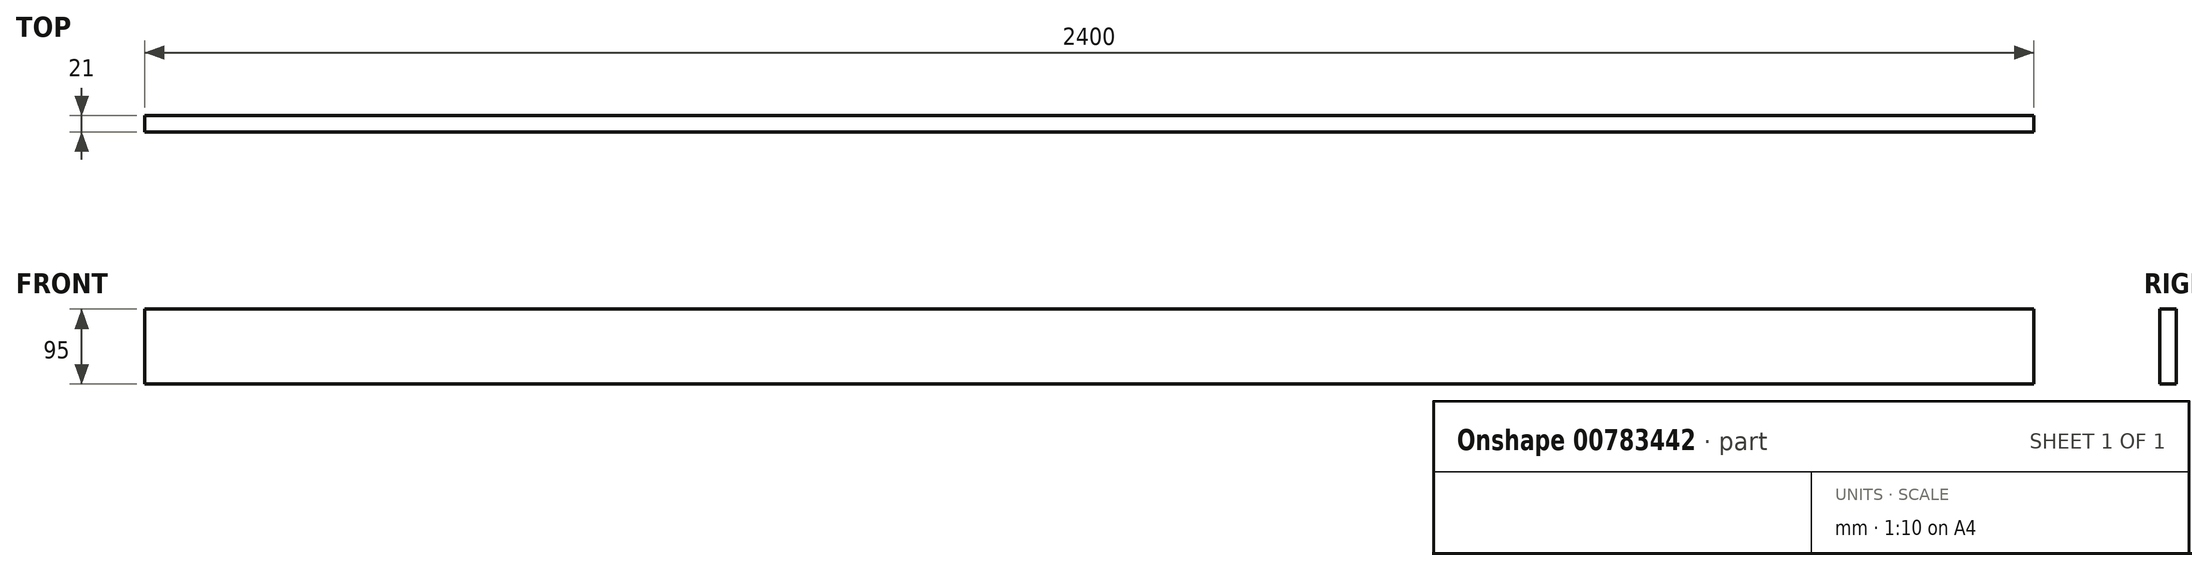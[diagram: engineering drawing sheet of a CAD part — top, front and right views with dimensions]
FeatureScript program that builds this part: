
annotation { "Feature Type Name" : "Feature", "Feature Type Description" : "" }
export const myFeature = defineFeature(function(context is Context, id is Id, definition is map)
    precondition{}
    {
        {
            var Q0;
            Q0=qCreatedBy(makeId("Front.planeOp"),FACE);
            var sketch = newSketch(context, id + "F0", { "sketchPlane" : qUnion([Q0])});
            skLineSegment(sketch, "E0.bottom", {"start": v(0, 0) * mm, "end": v(2400, 0) * mm});
            skLineSegment(sketch, "E0.top", {"start": v(0, 95) * mm, "end": v(2400, 95) * mm});
            skLineSegment(sketch, "E0.left", {"start": v(0, 0) * mm, "end": v(0, 95) * mm});
            skLineSegment(sketch, "E0.right", {"start": v(2400, 0) * mm, "end": v(2400, 95) * mm});
            skSolve(sketch);
        }
        {
            var Q0;
            Q0 = qSketchRegion(id + "F0", true);
            extrude(context, id + "F1", {"entities" : qUnion([Q0]), "depth" : 21 * mm, "offsetDistance" : 25 * mm});
        }
    });
